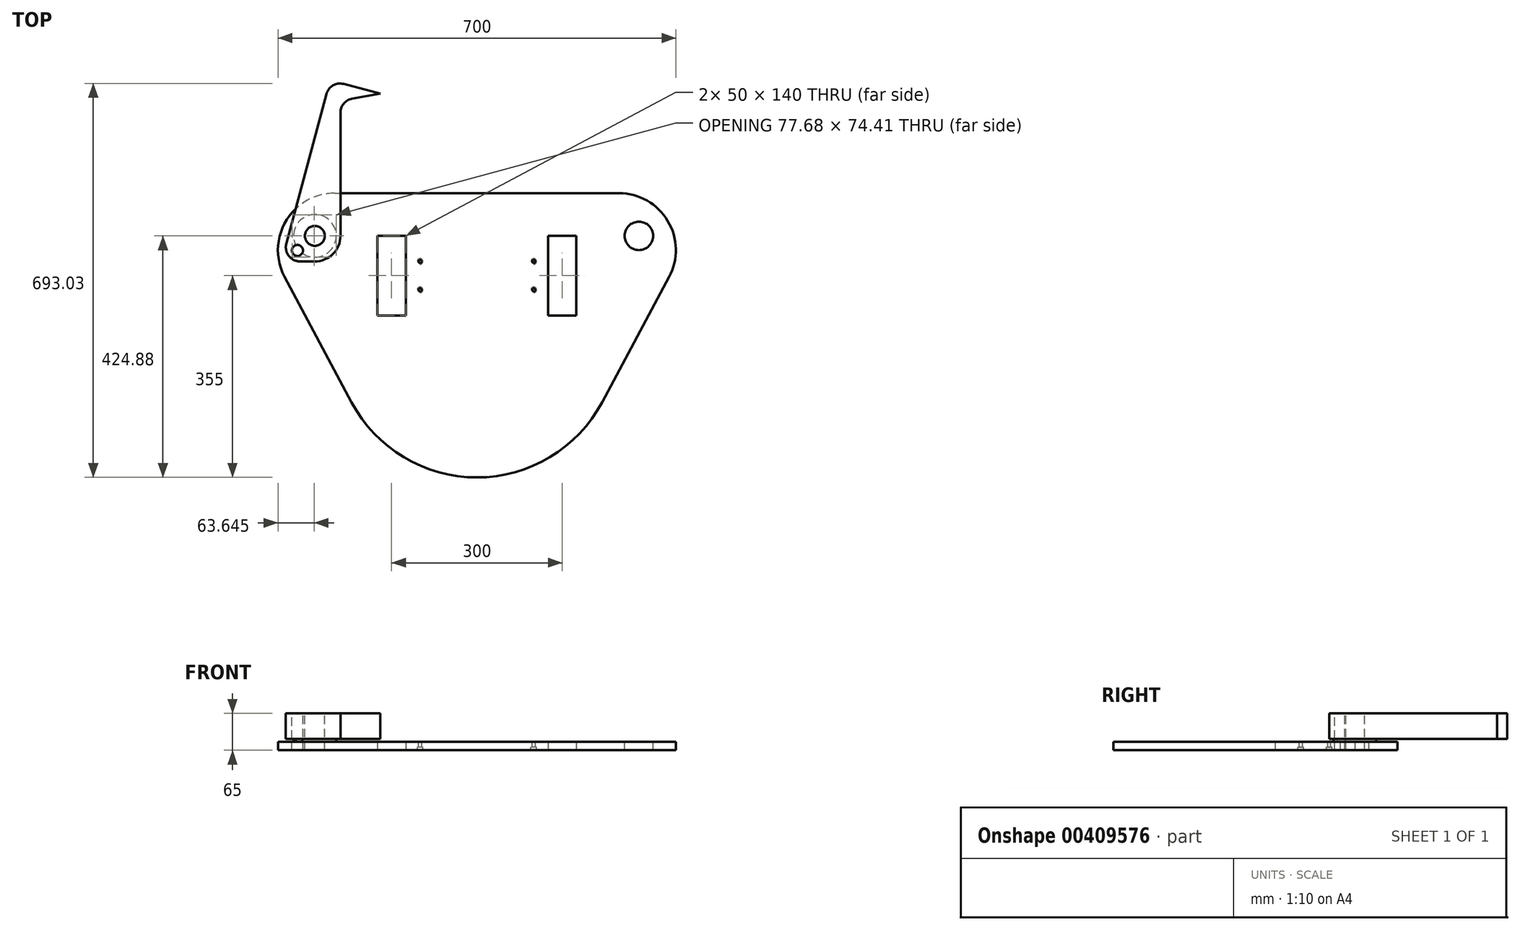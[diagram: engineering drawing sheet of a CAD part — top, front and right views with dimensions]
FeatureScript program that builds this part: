
annotation { "Feature Type Name" : "Feature", "Feature Type Description" : "" }
export const myFeature = defineFeature(function(context is Context, id is Id, definition is map)
    precondition{}
    {
        {
            var Q0;
            Q0=qCreatedBy(makeId("Top.planeOp"),FACE);
            var sketch = newSketch(context, id + "F0", { "sketchPlane" : qUnion([Q0])});
            skLineSegment(sketch, "E0.bottom", {"start": v(-175, -75) * mm, "end": v(-125, -75) * mm});
            skLineSegment(sketch, "E0.top", {"start": v(-175, -215) * mm, "end": v(-125, -215) * mm});
            skLineSegment(sketch, "E0.left", {"start": v(-175, -75) * mm, "end": v(-175, -215) * mm});
            skLineSegment(sketch, "E0.right", {"start": v(-125, -75) * mm, "end": v(-125, -215) * mm});
            skLineSegment(sketch, "E1.bottom", {"start": v(125, -75) * mm, "end": v(175, -75) * mm});
            skLineSegment(sketch, "E1.top", {"start": v(125, -215) * mm, "end": v(175, -215) * mm});
            skLineSegment(sketch, "E1.left", {"start": v(125, -75) * mm, "end": v(125, -215) * mm});
            skLineSegment(sketch, "E1.right", {"start": v(175, -75) * mm, "end": v(175, -215) * mm});
            skLineSegment(sketch, "E2", {"start": v(-250, 0) * mm, "end": v(250, 0) * mm});
            skArc(sketch, "E3", {"start": v(250, 0) * mm, "mid": v(335.75, -48.55) * mm, "end": v(338.24, -147.06) * mm});
            skLineSegment(sketch, "E4", {"start": v(338.24, -147.06) * mm, "end": v(220.59, -367.65) * mm});
            skLineSegment(sketch, "E5", {"start": v(-220.59, -367.65) * mm, "end": v(-338.24, -147.06) * mm});
            skArc(sketch, "E6.filletArc", {"start": v(-250, 0) * mm, "mid": v(-335.75, -48.55) * mm, "end": v(-338.24, -147.06) * mm});
            skArc(sketch, "E7.filletArc", {"start": v(-220.59, -367.65) * mm, "mid": v(0, -500) * mm, "end": v(220.59, -367.65) * mm});
            skSolve(sketch);
        }
        {
            var Q0;
            Q0=makeQuery(id+"F0.imprint","IMPRINT",FACE,{"disambiguationData":[TD([[makeQuery(id+"F0.imprint","IMPRINT",EDGE,{"derivedFrom":sQuery(id+"F0.wireOp",EDGE,"E0.bottom")}),1.0]])]});
            extrude(context, id + "F1", {"entities" : qUnion([Q0]), "depth" : 15 * mm, "offsetDistance" : 25 * mm});
        }
        {
            var Q0;
            Q0=makeQuery(id+"F1.opExtrude","CAP_FACE",FACE,{"disambiguationData":[OSD([sQuery(id+"F0.wireOp",EDGE,"E0.bottom"),sQuery(id+"F0.wireOp",EDGE,"E0.top"),sQuery(id+"F0.wireOp",EDGE,"E0.left"),sQuery(id+"F0.wireOp",EDGE,"E0.right"),sQuery(id+"F0.wireOp",EDGE,"E1.bottom"),sQuery(id+"F0.wireOp",EDGE,"E1.top"),sQuery(id+"F0.wireOp",EDGE,"E1.left"),sQuery(id+"F0.wireOp",EDGE,"E1.right"),sQuery(id+"F0.wireOp",EDGE,"E2"),sQuery(id+"F0.wireOp",EDGE,"E3"),sQuery(id+"F0.wireOp",EDGE,"E4"),sQuery(id+"F0.wireOp",EDGE,"E5"),sQuery(id+"F0.wireOp",EDGE,"E6.filletArc"),sQuery(id+"F0.wireOp",EDGE,"E7.filletArc")])],"isStart":false});
            var sketch = newSketch(context, id + "F2", { "sketchPlane" : qUnion([Q0])});
            skCircle(sketch, "E8", {"center": v(-285, -75) * mm, "radius": 25 * mm});
            skCircle(sketch, "E9", {"center": v(285, -75) * mm, "radius": 25 * mm});
            skSolve(sketch);
        }
        {
            var Q0;
            Q0 = qSketchRegion(id + "F2", true);
            extrude(context, id + "F3", {"entities" : qUnion([Q0]), "operationType" : NewBodyOperationType.REMOVE, "endBound" : BoundingType.THROUGH_ALL, "oppositeDirection" : true, "depth" : 25 * mm, "offsetDistance" : 25 * mm});
        }
        {
            var Q0;
            Q0=makeQuery(id+"F1.opExtrude","CAP_FACE",FACE,{"disambiguationData":[OSD([sQuery(id+"F0.wireOp",EDGE,"E0.bottom"),sQuery(id+"F0.wireOp",EDGE,"E0.top"),sQuery(id+"F0.wireOp",EDGE,"E0.left"),sQuery(id+"F0.wireOp",EDGE,"E0.right"),sQuery(id+"F0.wireOp",EDGE,"E1.bottom"),sQuery(id+"F0.wireOp",EDGE,"E1.top"),sQuery(id+"F0.wireOp",EDGE,"E1.left"),sQuery(id+"F0.wireOp",EDGE,"E1.right"),sQuery(id+"F0.wireOp",EDGE,"E2"),sQuery(id+"F0.wireOp",EDGE,"E3"),sQuery(id+"F0.wireOp",EDGE,"E4"),sQuery(id+"F0.wireOp",EDGE,"E5"),sQuery(id+"F0.wireOp",EDGE,"E6.filletArc"),sQuery(id+"F0.wireOp",EDGE,"E7.filletArc")])],"isStart":false});
            var sketch = newSketch(context, id + "F4", { "sketchPlane" : qUnion([Q0])});
            skCircle(sketch, "E10.0", {"center": v(-285, -75) * mm, "radius": 25 * mm});
            skCircle(sketch, "E11", {"center": v(-285, -75) * mm, "radius": 17.5 * mm});
            skSolve(sketch);
        }
        {
            var Q0;
            Q0=makeQuery(id+"F4.imprint","IMPRINT",FACE,{"disambiguationData":[TD([[makeQuery(id+"F4.imprint","IMPRINT",EDGE,{"derivedFrom":sQuery(id+"F4.wireOp",EDGE,"E10.0")}),1.0]])]});
            extrude(context, id + "F5", {"entities" : qUnion([Q0]), "oppositeDirection" : true, "depth" : 15 * mm, "offsetDistance" : 25 * mm});
        }
        {
            var Q0;
            Q0=makeQuery(id+"F5.opExtrude","CAP_FACE",FACE,{"disambiguationData":[OSD([sQuery(id+"F4.wireOp",EDGE,"E10.0"),sQuery(id+"F4.wireOp",EDGE,"E11")])],"isStart":true});
            var sketch = newSketch(context, id + "F6", { "sketchPlane" : qUnion([Q0])});
            skCircle(sketch, "E12.0", {"center": v(-285, -75) * mm, "radius": 17.5 * mm});
            skCircle(sketch, "E13", {"center": v(-285, -75) * mm, "radius": 37.5 * mm});
            skSolve(sketch);
        }
        {
            var Q0;
            Q0 = qSketchRegion(id + "F6", true);
            extrude(context, id + "F7", {"entities" : qUnion([Q0]), "operationType" : NewBodyOperationType.ADD, "depth" : 5 * mm, "offsetDistance" : 25 * mm});
        }
        {
            var Q0;
            Q0=makeQuery(id+"F1.opExtrude","CAP_FACE",FACE,{"disambiguationData":[OSD([sQuery(id+"F0.wireOp",EDGE,"E0.bottom"),sQuery(id+"F0.wireOp",EDGE,"E0.top"),sQuery(id+"F0.wireOp",EDGE,"E0.left"),sQuery(id+"F0.wireOp",EDGE,"E0.right"),sQuery(id+"F0.wireOp",EDGE,"E1.bottom"),sQuery(id+"F0.wireOp",EDGE,"E1.top"),sQuery(id+"F0.wireOp",EDGE,"E1.left"),sQuery(id+"F0.wireOp",EDGE,"E1.right"),sQuery(id+"F0.wireOp",EDGE,"E2"),sQuery(id+"F0.wireOp",EDGE,"E3"),sQuery(id+"F0.wireOp",EDGE,"E4"),sQuery(id+"F0.wireOp",EDGE,"E5"),sQuery(id+"F0.wireOp",EDGE,"E6.filletArc"),sQuery(id+"F0.wireOp",EDGE,"E7.filletArc")])],"isStart":true});
            var sketch = newSketch(context, id + "F8", { "sketchPlane" : qUnion([Q0])});
            skPoint(sketch, "E14", {"position": v(-100, 120) * mm});
            skPoint(sketch, "E15", {"position": v(-100, 170) * mm});
            skPoint(sketch, "E16", {"position": v(100, 170) * mm});
            skPoint(sketch, "E17", {"position": v(100, 120) * mm});
            skSolve(sketch);
        }
        {
            var Q0;
            Q0=sQuery(id+"F8.wireOp",VERTEX,"E14");
            var Q1;
            Q1=sQuery(id+"F8.wireOp",VERTEX,"E15");
            var Q2;
            Q2=sQuery(id+"F8.wireOp",VERTEX,"E17");
            var Q3;
            Q3=sQuery(id+"F8.wireOp",VERTEX,"E16");
            var Q4;
            Q4=makeQuery(id+"F1.opExtrude","SWEPT_BODY",BODY,{"disambiguationData":[OSD([sQuery(id+"F0.wireOp",EDGE,"E0.bottom"),sQuery(id+"F0.wireOp",EDGE,"E0.top"),sQuery(id+"F0.wireOp",EDGE,"E0.left"),sQuery(id+"F0.wireOp",EDGE,"E0.right"),sQuery(id+"F0.wireOp",EDGE,"E1.bottom"),sQuery(id+"F0.wireOp",EDGE,"E1.top"),sQuery(id+"F0.wireOp",EDGE,"E1.left"),sQuery(id+"F0.wireOp",EDGE,"E1.right"),sQuery(id+"F0.wireOp",EDGE,"E2"),sQuery(id+"F0.wireOp",EDGE,"E3"),sQuery(id+"F0.wireOp",EDGE,"E4"),sQuery(id+"F0.wireOp",EDGE,"E5"),sQuery(id+"F0.wireOp",EDGE,"E6.filletArc"),sQuery(id+"F0.wireOp",EDGE,"E7.filletArc")])]});
            hole(context, id + "F9", {"style" : HoleStyle.C_BORE, "endStyle" : HoleEndStyle.THROUGH, "standardTappedOrClearance" : lookupTablePath({ "fit" : "Normal", "standard" : "ISO", "size" : "M5", "type" : "Clearance" }), "standardBlindInLast" : lookupTablePath({ "fit" : "Normal", "standard" : "ISO", "engagement" : "75%", "pitch" : "0.8 mm", "size" : "M5", "type" : "Clearance & tapped" }), "holeDiameter" : 5.5 * mm, "cBoreDiameter" : 9.75 * mm, "cBoreDepth" : 5 * mm, "majorDiameter" : 5 * mm, "isTappedThrough" : true, "tappedDepth" : 12 * mm, "tapClearance" : 3, "locations" : qUnion([Q0, Q1, Q2, Q3]), "scope" : qUnion([Q4])});
        }
        {
            var Q0;
            Q0=makeQuery(id+"F7.opExtrude","CAP_FACE",FACE,{"disambiguationData":[OSD([sQuery(id+"F6.wireOp",EDGE,"E12.0"),sQuery(id+"F6.wireOp",EDGE,"E13")])],"isStart":false});
            var sketch = newSketch(context, id + "F10", { "sketchPlane" : qUnion([Q0])});
            skCircle(sketch, "E18", {"center": v(-285, -75) * mm, "radius": 45 * mm});
            skCircle(sketch, "E19", {"center": v(-285, -75) * mm, "radius": 17.5 * mm});
            skSolve(sketch);
        }
        {
            var Q0;
            Q0 = qSketchRegion(id + "F10", true);
            var Q1;
            Q1=sQuery(id+"F10.wireOp",EDGE,"E18");
            extrude(context, id + "F11", {"entities" : qUnion([Q0]), "surfaceEntities" : qUnion([Q1]), "depth" : 45 * mm, "offsetDistance" : 25 * mm});
        }
        {
            var Q0;
            Q0=makeQuery(id+"F11.opExtrude","CAP_FACE",FACE,{"disambiguationData":[OSD([sQuery(id+"F10.wireOp",EDGE,"E18")])],"isStart":true});
            var sketch = newSketch(context, id + "F12", { "sketchPlane" : qUnion([Q0])});
            skArc(sketch, "E20.0", {"start": v(-240, 75) * mm, "mid": v(-253.18, 106.82) * mm, "end": v(-285, 120) * mm});
            skLineSegment(sketch, "E21", {"start": v(-343.65, 120) * mm, "end": v(-258.26, -198.65) * mm});
            skLineSegment(sketch, "E22", {"start": v(-258.26, -198.65) * mm, "end": v(-170, -175) * mm});
            skLineSegment(sketch, "E23", {"start": v(-170, -175) * mm, "end": v(-240, -162.66) * mm});
            skLineSegment(sketch, "E24", {"start": v(-240, -162.66) * mm, "end": v(-240, 75) * mm});
            skLineSegment(sketch, "E25", {"start": v(-240, 75) * mm, "end": v(-285, 75) * mm, "construction": true});
            skCircle(sketch, "E26.0", {"center": v(-285, 75) * mm, "radius": 17.5 * mm});
            skLineSegment(sketch, "E27", {"start": v(-285, 120) * mm, "end": v(-343.65, 120) * mm});
            skLineSegment(sketch, "E28", {"start": v(-285, 75) * mm, "end": v(-285, 120) * mm, "construction": true});
            skLineSegment(sketch, "E29", {"start": v(-285, 120) * mm, "end": v(-285, 120) * mm});
            skSolve(sketch);
        }
        {
            var Q0;
            Q0 = qSketchRegion(id + "F12", true);
            var Q1;
            Q1=makeQuery(id+"F11.opExtrude","CAP_FACE",FACE,{"disambiguationData":[OSD([sQuery(id+"F10.wireOp",EDGE,"E18")])],"isStart":false});
            extrude(context, id + "F13", {"entities" : qUnion([Q0]), "operationType" : NewBodyOperationType.ADD, "endBound" : BoundingType.UP_TO_SURFACE, "oppositeDirection" : true, "depth" : 25 * mm, "endBoundEntityFace" : qUnion([Q1]), "offsetDistance" : 25 * mm});
        }
        {
            var Q0;
            Q0=makeQuery(id+"F13.boolean.opBoolean","MERGE",FACE,{"derivedFrom":[makeQuery(id+"F11.opExtrude","CAP_FACE",FACE,{"disambiguationData":[OSD([sQuery(id+"F10.wireOp",EDGE,"E18"),sQuery(id+"F10.wireOp",EDGE,"E19")])],"isStart":false}),makeQuery(id+"F13.opExtrude","CAP_FACE",FACE,{"disambiguationData":[OSD([sQuery(id+"F12.wireOp",EDGE,"E20.0"),sQuery(id+"F12.wireOp",EDGE,"E21"),sQuery(id+"F12.wireOp",EDGE,"E22"),sQuery(id+"F12.wireOp",EDGE,"E23"),sQuery(id+"F12.wireOp",EDGE,"E24"),sQuery(id+"F12.wireOp",EDGE,"E26.0"),sQuery(id+"F12.wireOp",EDGE,"E27")])],"isStart":false})]});
            var sketch = newSketch(context, id + "F14", { "sketchPlane" : qUnion([Q0])});
            skCircle(sketch, "E30", {"center": v(-315.64, -100.71) * mm, "radius": 9.77 * mm});
            skLineSegment(sketch, "E31", {"start": v(-285, -75) * mm, "end": v(-315.64, -100.71) * mm, "construction": true});
            skSolve(sketch);
        }
        {
            var Q0;
            Q0=makeQuery(id+"F14.imprint","IMPRINT",FACE,{"disambiguationData":[TD([[makeQuery(id+"F14.imprint","IMPRINT",EDGE,{"derivedFrom":sQuery(id+"F14.wireOp",EDGE,"E30")}),1.0]])]});
            extrude(context, id + "F15", {"entities" : qUnion([Q0]), "operationType" : NewBodyOperationType.REMOVE, "endBound" : BoundingType.THROUGH_ALL, "oppositeDirection" : true, "depth" : 25 * mm, "offsetDistance" : 25 * mm});
        }
        {
            var Q0;
            Q0=makeQuery(id+"F13.opExtrude","SWEPT_EDGE",EDGE,{"disambiguationData":[OSD([sQuery(id+"F12.wireOp",EDGE,"E23"),sQuery(id+"F12.wireOp",EDGE,"E24")])]});
            var Q1;
            Q1=makeQuery(id+"F13.opExtrude","SWEPT_EDGE",EDGE,{"disambiguationData":[OSD([sQuery(id+"F12.wireOp",EDGE,"E21"),sQuery(id+"F12.wireOp",EDGE,"E22")])]});
            var Q2;
            Q2=makeQuery(id+"F13.opExtrude","SWEPT_EDGE",EDGE,{"disambiguationData":[OSD([sQuery(id+"F12.wireOp",EDGE,"E21"),sQuery(id+"F12.wireOp",EDGE,"E27")])]});
            fillet(context, id + "F16", {"entities" : qUnion([Q0, Q1, Q2]), "tangentPropagation" : true, "radius" : 25 * mm, "defaultsChanged" : true, "vertexSettings" : [], "allowEdgeOverflow" : false});
        }
    });
